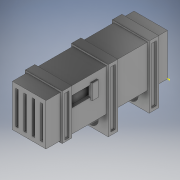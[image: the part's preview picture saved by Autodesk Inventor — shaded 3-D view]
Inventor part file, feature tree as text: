
AUTODESK INVENTOR PART (.ipt)
format: ipt  version: 2021 (Build 250183000, 183)  size: 695,808 bytes
history: native  units: mm
features: sketch x20, extrude x15, plane x1
ambient origin geometry x8: Origin, YZ Plane, XZ Plane, XY Plane, X Axis, Y Axis, Z Axis, Center Point
bodies: Solid1 (feature_tree)
feature tree (36):
  extrude  "Extrusion1"  Depth=50.8mm
  extrude  "Extrusion2"  Depth=3.742mm
  sketch  "Sketch3"  dims[d5=50.292mm d6=5.021mm]
  plane  "Work Plane1"
  extrude  "Extrusion3"  Depth=5.021mm
  sketch  "Sketch4"  dims[d7=6.604mm d8=8.704mm]
  extrude  "Extrusion4"  Depth=8.704mm
  extrude  "Extrusion5"  Depth=3.742mm
  extrude  "Extrusion6"  Depth=8.704mm
  sketch  "Sketch8"  dims[d17=100.0mm d18=0.0mm d19=94.707mm]
  extrude  "Extrusion7"  Depth=8.704mm
  sketch  "Sketch10"  dims[d22=2.54mm d23=94.707mm d24=14.463mm]
  sketch  "Sketch11"  dims[d25=68.58mm d26=14.463mm d27=2.54mm d28=2.54mm]
  extrude  "Extrusion8"  Depth=94.707mm
  extrude  "Extrusion9"  Depth=15.895mm
  extrude  "Extrusion10"  Depth=94.707mm
  sketch  "Sketch13"  dims[d31=2.54mm d32=55.88mm d33=0.0mm]
  extrude  "Extrusion11"  Depth=2.54mm
  extrude  "Extrusion12"  Depth=55.369mm
  extrude  "Extrusion13"  Depth=55.88mm TaperAngle=0.0deg
  extrude  "Extrusion14"  Depth=85.239mm
  sketch  "Sketch18"  dims[d41=4.53mm]
  sketch  "Sketch19"  dims[d42=61.42mm]
  extrude  "Extrusion15"  Depth=6.982mm
  sketch  "Sketch1"  dims[d0=63.5mm d1=50.8mm]
  sketch  "Sketch2"  dims[d2=184.15mm d3=0.0mm d4=3.742mm]
  sketch  "Sketch5"  dims[d9=6.604mm d10=3.742mm]
  sketch  "Sketch6"  dims[d11=3.742mm d12=8.704mm]
  sketch  "Sketch7"  dims[d13=3.742mm d16=8.704mm]
  sketch  "Sketch9"  dims[d20=14.463mm d21=15.895mm]
  sketch  "Sketch12"  dims[d29=47.547mm d30=55.369mm]
  sketch  "Sketch14"  dims[d34=6.982mm d35=85.239mm]
  sketch  "Sketch15"  dims[d36=3.725mm d37=6.982mm d38=85.239mm]
  sketch  "Sketch16"  dims[d39=3.725mm]
  sketch  "Sketch17"  dims[d40=4.53mm]
  sketch  "Sketch20"  dims[d43=5.881mm d44=4.287mm d45=2.54mm d46=0.0mm d48=9.417mm d49=14.937mm d50=9.819mm d51=22.975mm d52=1.905mm d53=0.0mm d54=13.021mm d55=16.131mm d56=6.926mm d57=0.0mm d58=16.131mm d59=1.905mm d60=9.417mm d61=0.0mm d62=27.142mm d63=14.282mm d64=24.181mm d65=24.181mm d66=14.282mm d67=27.142mm d68=30.0mm d69=0.0mm d70=30.0mm d71=0.0mm d72=0.127mm d73=0.684mm d74=24.765mm d75=500.0mm d76=0.0mm d77=31.015mm d80=9.819mm d81=9.417mm d82=22.975mm d83=5.021mm d84=0.0mm d85=16.131mm d86=13.021mm d87=5.021mm d88=0.0mm d89=16.131mm d90=1.905mm d91=9.417mm d92=0.0mm d93=10.502mm d94=10.502mm d95=6.507mm d96=21.312mm d97=6.507mm d98=10.502mm d99=10.502mm d100=21.312mm d101=2.54mm d102=0.0mm d103=5.881mm d104=61.42mm d105=4.62mm d106=4.295mm d107=6.982mm d108=85.239mm d109=4.938mm d110=3.725mm d111=6.982mm d112=85.239mm d113=4.938mm d114=3.725mm d115=2.54mm d116=0.0mm d78=0.872665mm]
